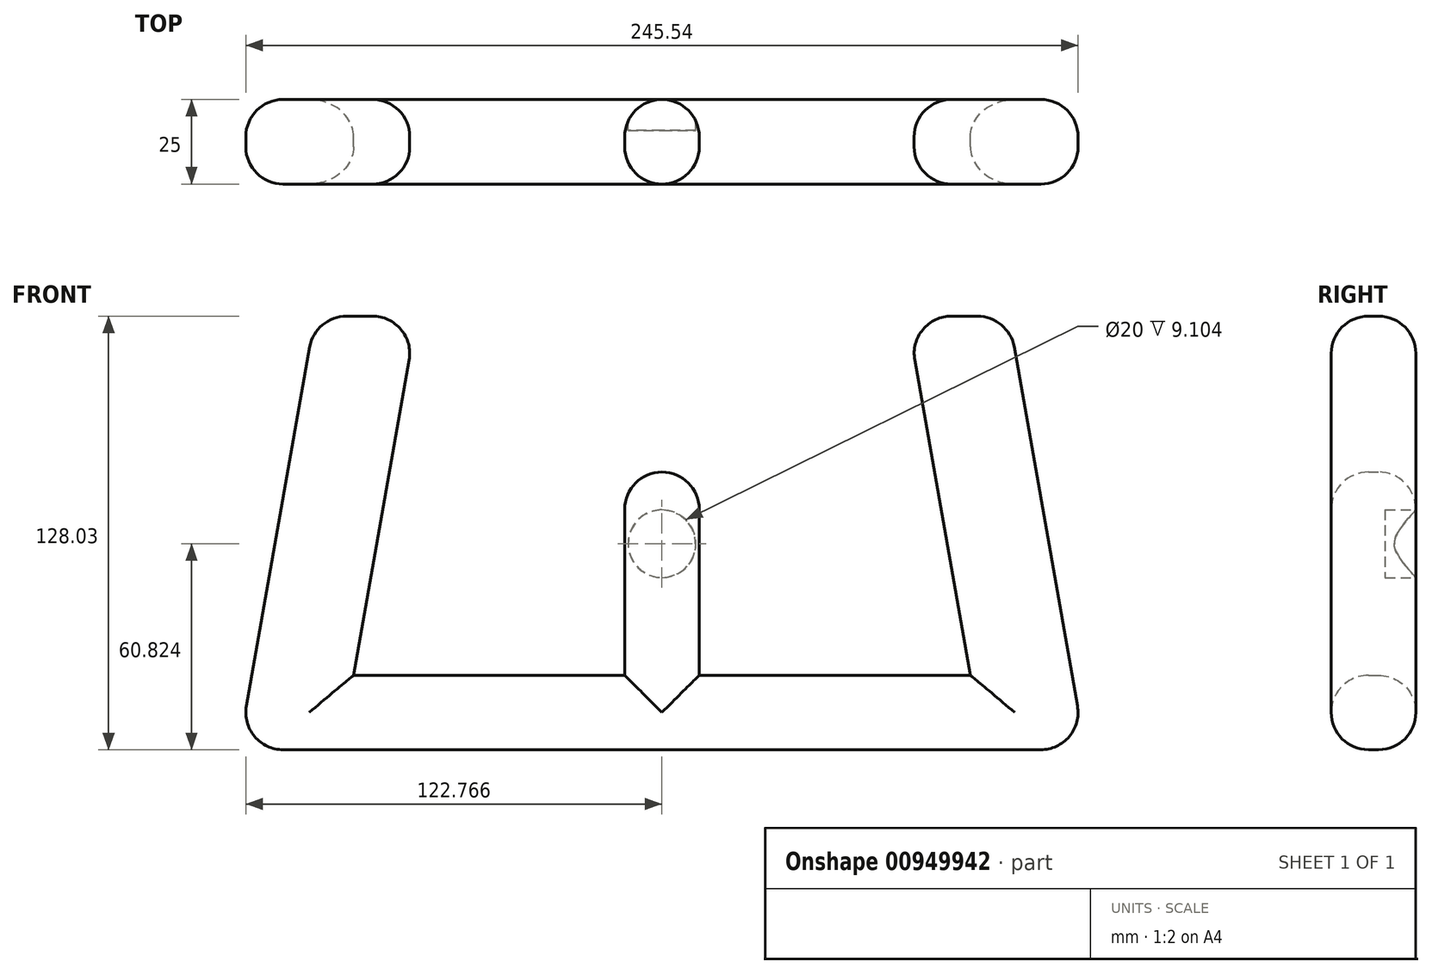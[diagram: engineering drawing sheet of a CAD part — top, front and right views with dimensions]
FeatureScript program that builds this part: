
annotation { "Feature Type Name" : "Feature", "Feature Type Description" : "" }
export const myFeature = defineFeature(function(context is Context, id is Id, definition is map)
    precondition{}
    {
        {
            var Q0;
            Q0=qCreatedBy(makeId("Front.planeOp"),FACE);
            var sketch = newSketch(context, id + "F0", { "sketchPlane" : qUnion([Q0])});
            skLineSegment(sketch, "E0", {"start": v(-127.32, 0) * mm, "end": v(122.44, 0) * mm});
            skLineSegment(sketch, "E1", {"start": v(-104.74, 128.03) * mm, "end": v(-93.57, 128.03) * mm});
            skLineSegment(sketch, "E2", {"start": v(-93.44, 22) * mm, "end": v(-13.44, 22) * mm});
            skLineSegment(sketch, "E3", {"start": v(-13.44, 22) * mm, "end": v(-13.44, 82) * mm});
            skLineSegment(sketch, "E4", {"start": v(-13.44, 82) * mm, "end": v(8.56, 82) * mm});
            skLineSegment(sketch, "E5", {"start": v(8.56, 82) * mm, "end": v(8.56, 22) * mm});
            skLineSegment(sketch, "E6", {"start": v(8.56, 22) * mm, "end": v(88.56, 22) * mm});
            skLineSegment(sketch, "E7", {"start": v(92.56, 128.03) * mm, "end": v(99.87, 128.03) * mm});
            skLineSegment(sketch, "E8", {"start": v(88.56, 22) * mm, "end": v(69.87, 128.03) * mm});
            skLineSegment(sketch, "E9", {"start": v(69.87, 128.03) * mm, "end": v(99.87, 128.03) * mm});
            skLineSegment(sketch, "E10", {"start": v(99.87, 128.03) * mm, "end": v(122.44, 0) * mm});
            skLineSegment(sketch, "E11", {"start": v(-93.44, 22) * mm, "end": v(-74.74, 128.03) * mm});
            skLineSegment(sketch, "E12", {"start": v(-74.74, 128.03) * mm, "end": v(-104.74, 128.03) * mm});
            skLineSegment(sketch, "E13", {"start": v(-104.74, 128.03) * mm, "end": v(-127.32, 0) * mm});
            skSolve(sketch);
        }
        {
            var Q0;
            Q0 = qSketchRegion(id + "F0", true);
            extrude(context, id + "F1", {"entities" : qUnion([Q0]), "depth" : 25 * mm, "offsetDistance" : 25 * mm});
        }
        {
            var Q0;
            Q0=makeQuery(id+"F1.opExtrude","CAP_FACE",FACE,{"disambiguationData":[OSD([sQuery(id+"F0.wireOp",EDGE,"E0"),sQuery(id+"F0.wireOp",EDGE,"xIxTfvJY-XZiJ-qPEi-egHz-keXieLPRNhWQ"),sQuery(id+"F0.wireOp",EDGE,"JTNpAG1x-L98s-bi4T-tOLY-zrfycqL7UQJ5"),sQuery(id+"F0.wireOp",EDGE,"E1"),sQuery(id+"F0.wireOp",EDGE,"OvWzpCb6-HYhU-zQ6t-oPC1-ooGUEtrQsgqX"),sQuery(id+"F0.wireOp",EDGE,"E2"),sQuery(id+"F0.wireOp",EDGE,"E3"),sQuery(id+"F0.wireOp",EDGE,"E4"),sQuery(id+"F0.wireOp",EDGE,"E5"),sQuery(id+"F0.wireOp",EDGE,"E6"),sQuery(id+"F0.wireOp",EDGE,"AnAH884Z-1ipk-Ae1e-VJOd-Xi6cuUZr1hVg"),sQuery(id+"F0.wireOp",EDGE,"E7")])],"isStart":false});
            var Q1;
            Q1=makeQuery(id+"F1.opExtrude","CAP_FACE",FACE,{"disambiguationData":[OSD([sQuery(id+"F0.wireOp",EDGE,"E0"),sQuery(id+"F0.wireOp",EDGE,"xIxTfvJY-XZiJ-qPEi-egHz-keXieLPRNhWQ"),sQuery(id+"F0.wireOp",EDGE,"JTNpAG1x-L98s-bi4T-tOLY-zrfycqL7UQJ5"),sQuery(id+"F0.wireOp",EDGE,"E1"),sQuery(id+"F0.wireOp",EDGE,"OvWzpCb6-HYhU-zQ6t-oPC1-ooGUEtrQsgqX"),sQuery(id+"F0.wireOp",EDGE,"E2"),sQuery(id+"F0.wireOp",EDGE,"E3"),sQuery(id+"F0.wireOp",EDGE,"E4"),sQuery(id+"F0.wireOp",EDGE,"E5"),sQuery(id+"F0.wireOp",EDGE,"E6"),sQuery(id+"F0.wireOp",EDGE,"AnAH884Z-1ipk-Ae1e-VJOd-Xi6cuUZr1hVg"),sQuery(id+"F0.wireOp",EDGE,"E7")])],"isStart":true});
            var Q2;
            Q2=makeQuery(id+"F1.opExtrude","SWEPT_FACE",FACE,{"disambiguationData":[OSD([sQuery(id+"F0.wireOp",EDGE,"E1")])]});
            var Q3;
            Q3=makeQuery(id+"F1.opExtrude","SWEPT_FACE",FACE,{"disambiguationData":[OSD([sQuery(id+"F0.wireOp",EDGE,"E4")])]});
            var Q4;
            Q4=makeQuery(id+"F1.opExtrude","SWEPT_FACE",FACE,{"disambiguationData":[OSD([sQuery(id+"F0.wireOp",EDGE,"E7")])]});
            var Q5;
            Q5=makeQuery(id+"F1.opExtrude","SWEPT_EDGE",EDGE,{"disambiguationData":[OSD([sQuery(id+"F0.wireOp",EDGE,"E0"),sQuery(id+"F0.wireOp",EDGE,"JTNpAG1x-L98s-bi4T-tOLY-zrfycqL7UQJ5")])]});
            var Q6;
            Q6=makeQuery(id+"F1.opExtrude","SWEPT_EDGE",EDGE,{"disambiguationData":[OSD([sQuery(id+"F0.wireOp",EDGE,"E0"),sQuery(id+"F0.wireOp",EDGE,"xIxTfvJY-XZiJ-qPEi-egHz-keXieLPRNhWQ")])]});
            fillet(context, id + "F2", {"entities" : qUnion([Q0, Q1, Q2, Q3, Q4, Q5, Q6]), "tangentPropagation" : true, "radius" : 11 * mm, "defaultsChanged" : true, "vertexSettings" : [], "allowEdgeOverflow" : false});
        }
        {
            var Q0;
            Q0=qCreatedBy(makeId("Front.planeOp"),FACE);
            var sketch = newSketch(context, id + "F3", { "sketchPlane" : qUnion([Q0])});
            skCircle(sketch, "E14", {"center": v(-2.44, 60.82) * mm, "radius": 10 * mm});
            skSolve(sketch);
        }
        {
            var Q0;
            Q0 = qSketchRegion(id + "F3", true);
            extrude(context, id + "F4", {"entities" : qUnion([Q0]), "operationType" : NewBodyOperationType.REMOVE, "depth" : 9.1 * mm, "offsetDistance" : 25 * mm});
        }
    });
